# Revit family: P4TT, 1812
name_source: partatom
category: Windows
revit_build: Autodesk Revit LT 2016 (Build: 20150220_1215(x64)
units: mm (PartAtom-declared; Revit-internal decimal feet)

## family parameters
Always vertical = Yes
Cut with Voids When Loaded = No
Host = Wall
OmniClass Number = 23.30.20.00
OmniClass Title = Windows
Room Calculation Point = No
Shared = No

## types (1)
- P4TT Type- 1812
    Aluminium anodized = Aluminium
    Bottom fixed glass width = 6 mm  [stored 0.019685 ft]
    Centre fixed glass width = 6 mm  [stored 0.019685 ft]
    Centre vert mullion = 610 mm  [stored 2.00131 ft]
    Default Sill Height = 914 mm
    Description = Anodized Aluminium
    Glazing = Glass
    Height = 1210 mm  [stored 3.96982 ft]
    Manufacturer = Robmeg
    Model = P4TT 1812
    Plaster = 5 mm  [stored 0.0164042 ft]
    Rough Height = 1219 mm
    Top hung = Yes
    Top mullion = 600 mm
    URL = http://www.robmeg.co.za
    Wall Closure = By host
    Width = 1810 mm  [stored 5.93832 ft]

note: [stored X ft] marks values corroborated as IEEE doubles in the binary element streams (Revit-internal decimal feet)

## geometry (parser evidence)
native form markers: Sweep x3
no freeform markers — native parametric forms only
